# Revit family: Toilet_Universal_Bowl-Everclean-American_Standard-Huron-331x_Series
name_source: partatom
category: Plumbing Fixtures
revit_build: Autodesk Revit 2014 (Build: 20130308_1515(x64)
units: mm (PartAtom-declared; Revit-internal decimal feet)

## types (2) — shared parameters
ADA Compliant = Yes
Assembly Code = D2010110
Bowl Shape = Elongated
CW Connection = Yes
CWFU = 5
Cold Water Connection Diameter = 1 1/2"
Cold Water Connection Radius = 3/4"
Default Elevation = 0"
Flush Rate = 1.28 gpf to 1.6 gpf (4.8 Lpf to 6.0 Lpf)
HW Connection = No
Height = 17 1/8"
Installation Type = Floor Mounted
Length = 24 7/8"
Manufacturer = American Standard
Material = Vitreous China-American Standard-020-White
Price = Prices may vary. Please consult Manufacturer Representative for most up-to-date price list.
Product Documentation Link = https://www.americanstandard-us.com
Product Page URL = http://www.americanstandard-us.com
Revised Date = 08/09/2016
URL = http://www.americanstandard-us.com
Vent Connection = No
WFU = 5
Warranty Information = 2-Year Warranty
Waste Connection = Yes
Waste Connection Diameter = 2 1/8"
Waste Connection Radius = 1 1/16"
Width = 13 3/4"
zero-valued in all types: HWFU

## per-type parameters (varying)
| type | Description | Visible | Void Visibility |
| 3312.001 | Huron Universal Bowl With Everclean. Top spud, wall outlet. | No | 12" |
| 3313.001 | Huron Universal Bowl With Everclean. Top spud, wall outlet, with bed pan lugs. | Yes | 18" |

note: column(s) folded — value = type name in every type: Model

## geometry (parser evidence)
native form markers: Sweep x5
no freeform markers — native parametric forms only
